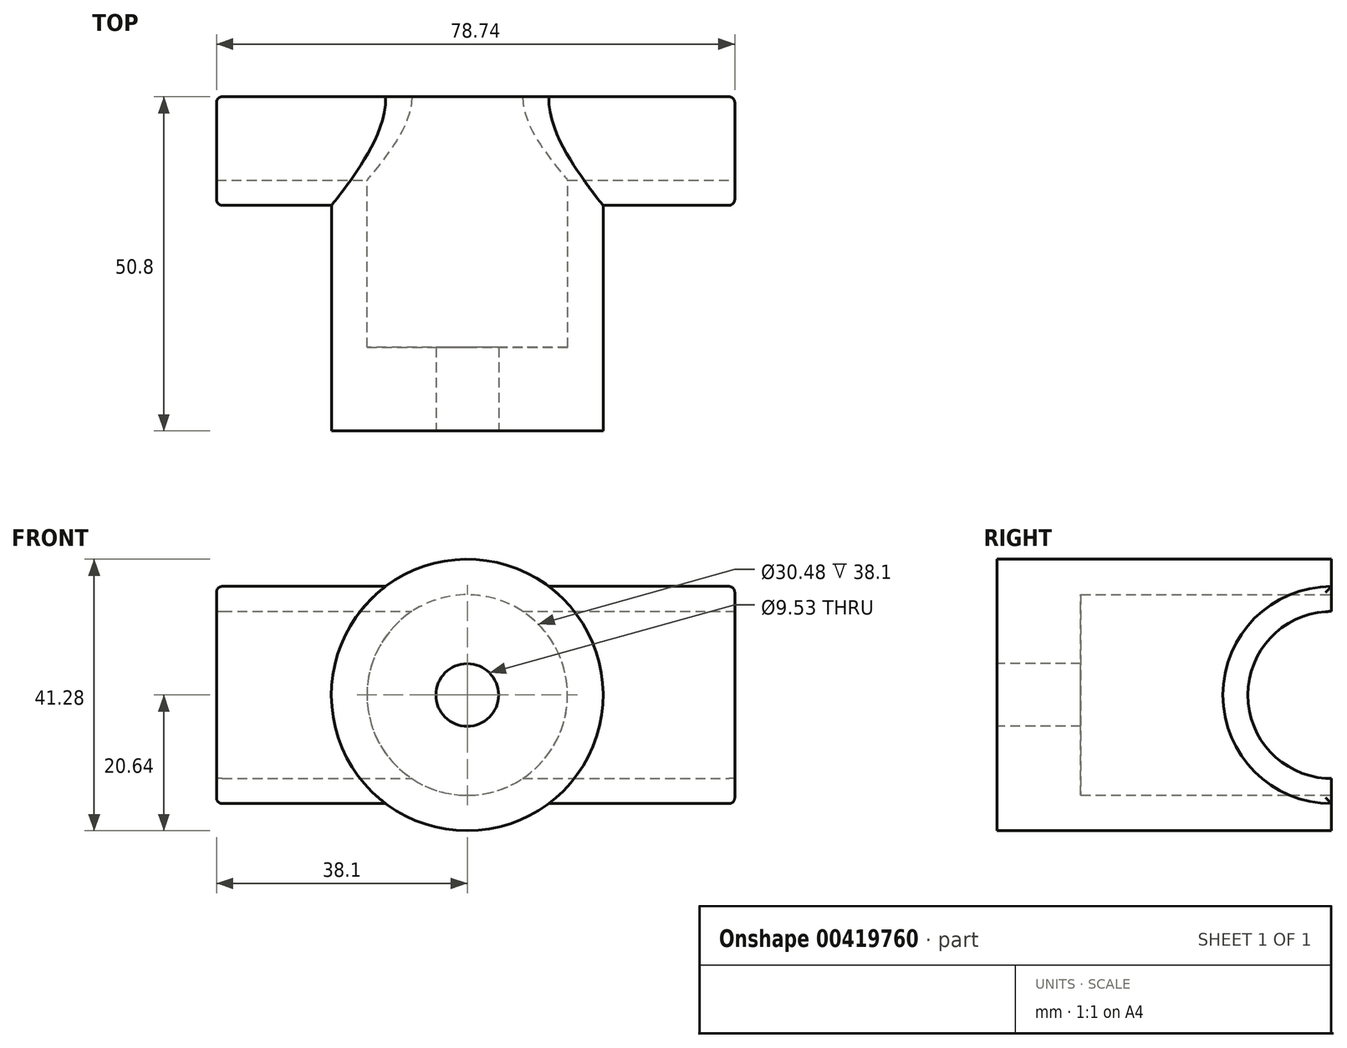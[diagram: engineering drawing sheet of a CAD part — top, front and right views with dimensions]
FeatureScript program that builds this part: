
annotation { "Feature Type Name" : "Feature", "Feature Type Description" : "" }
export const myFeature = defineFeature(function(context is Context, id is Id, definition is map)
    precondition{}
    {
        {
            var Q0;
            Q0=qCreatedBy(makeId("Front.planeOp"),FACE);
            var sketch = newSketch(context, id + "F0", { "sketchPlane" : qUnion([Q0])});
            skCircle(sketch, "E0", {"center": v(0, 0) * mm, "radius": 20.64 * mm});
            skSolve(sketch);
        }
        {
            var Q0;
            Q0 = qSketchRegion(id + "F0", true);
            extrude(context, id + "F1", {"entities" : qUnion([Q0]), "depth" : 50.8 * mm});
        }
        {
            var Q0;
            Q0=qCreatedBy(makeId("Right.planeOp"),FACE);
            cPlane(context, id + "F2", {"entities" : qUnion([Q0]), "cplaneType" : CPlaneType.OFFSET, "offset" : 40.64 * mm, "width" : 152.4 * mm, "height" : 152.4 * mm});
        }
        {
            var Q0;
            Q0=qCreatedBy(id+"F2.planeOp",FACE);
            var sketch = newSketch(context, id + "F3", { "sketchPlane" : qUnion([Q0])});
            skArc(sketch, "E1", {"start": v(0, 16.51) * mm, "mid": v(-16.51, 0) * mm, "end": v(0, -16.51) * mm});
            skArc(sketch, "E2", {"start": v(0, 12.7) * mm, "mid": v(-12.7, 0) * mm, "end": v(0, -12.7) * mm});
            skLineSegment(sketch, "E3", {"start": v(0, 16.51) * mm, "end": v(0, 12.7) * mm});
            skPoint(sketch, "E4.orphan", {"position": v(0, 24.9) * mm});
            skLineSegment(sketch, "E5.trimOffspring", {"start": v(0, -12.7) * mm, "end": v(0, -16.51) * mm});
            skSolve(sketch);
        }
        {
            var Q0;
            Q0=makeQuery(id+"F3.imprint","IMPRINT",FACE,{"disambiguationData":[TD([[makeQuery(id+"F3.imprint","IMPRINT",EDGE,{"derivedFrom":sQuery(id+"F3.wireOp",EDGE,"E1")}),1.0]])]});
            extrude(context, id + "F4", {"entities" : qUnion([Q0]), "operationType" : NewBodyOperationType.ADD, "oppositeDirection" : true, "depth" : 78.74 * mm});
        }
        {
            var Q0;
            Q0=qCreatedBy(makeId("Front.planeOp"),FACE);
            var sketch = newSketch(context, id + "F5", { "sketchPlane" : qUnion([Q0])});
            skCircle(sketch, "E6", {"center": v(0, 0) * mm, "radius": 15.24 * mm});
            skSolve(sketch);
        }
        {
            var Q0;
            Q0=makeQuery(id+"F5.imprint","IMPRINT",FACE,{"disambiguationData":[TD([[makeQuery(id+"F5.imprint","IMPRINT",EDGE,{"derivedFrom":sQuery(id+"F5.wireOp",EDGE,"E6")}),1.0]])]});
            extrude(context, id + "F6", {"entities" : qUnion([Q0]), "operationType" : NewBodyOperationType.REMOVE, "depth" : 38.1 * mm});
        }
        {
            var Q0;
            Q0=qCreatedBy(id+"F2.planeOp",FACE);
            var sketch = newSketch(context, id + "F7", { "sketchPlane" : qUnion([Q0])});
            skArc(sketch, "E7", {"start": v(0, 12.7) * mm, "mid": v(-12.7, 0) * mm, "end": v(0, -12.7) * mm});
            skPoint(sketch, "E8.orphan", {"position": v(0, 24.9) * mm});
            skLineSegment(sketch, "E9", {"start": v(0, 12.7) * mm, "end": v(0, -12.7) * mm});
            skSolve(sketch);
        }
        {
            var Q0;
            Q0=makeQuery(id+"F7.imprint","IMPRINT",FACE,{"disambiguationData":[TD([[makeQuery(id+"F7.imprint","IMPRINT",EDGE,{"derivedFrom":sQuery(id+"F7.wireOp",EDGE,"E7")}),1.0]])]});
            extrude(context, id + "F8", {"entities" : qUnion([Q0]), "operationType" : NewBodyOperationType.REMOVE, "endBound" : BoundingType.THROUGH_ALL, "oppositeDirection" : true, "depth" : 25.4 * mm});
        }
        {
            var Q0;
            Q0=makeQuery(id+"F1.opExtrude","CAP_FACE",FACE,{"disambiguationData":[OSD([sQuery(id+"F0.wireOp",EDGE,"E0")])],"isStart":false});
            var sketch = newSketch(context, id + "F9", { "sketchPlane" : qUnion([Q0])});
            skCircle(sketch, "E10", {"center": v(0, 0) * mm, "radius": 4.76 * mm});
            skSolve(sketch);
        }
        {
            var Q0;
            Q0 = qSketchRegion(id + "F9", true);
            extrude(context, id + "F10", {"entities" : qUnion([Q0]), "operationType" : NewBodyOperationType.REMOVE, "endBound" : BoundingType.THROUGH_ALL, "oppositeDirection" : true, "depth" : 25.4 * mm});
        }
        {
            var Q0;
            Q0=makeQuery(id+"F4.opExtrude","CAP_EDGE",EDGE,{"disambiguationData":[OSD([sQuery(id+"F3.wireOp",EDGE,"E5.trimOffspring")])],"isStart":false});
            var Q1;
            Q1=makeQuery(id+"F4.opExtrude","CAP_EDGE",EDGE,{"disambiguationData":[OSD([sQuery(id+"F3.wireOp",EDGE,"E3")])],"isStart":false});
            var Q2;
            Q2=makeQuery(id+"F4.opExtrude","CAP_EDGE",EDGE,{"disambiguationData":[OSD([sQuery(id+"F3.wireOp",EDGE,"E5.trimOffspring")])],"isStart":true});
            var Q3;
            Q3=makeQuery(id+"F4.opExtrude","CAP_EDGE",EDGE,{"disambiguationData":[OSD([sQuery(id+"F3.wireOp",EDGE,"E3")])],"isStart":true});
            var Q4;
            Q4=makeQuery(id+"F4.opExtrude","CAP_EDGE",EDGE,{"disambiguationData":[OSD([sQuery(id+"F3.wireOp",EDGE,"E1")])],"isStart":false});
            var Q5;
            Q5=makeQuery(id+"F4.opExtrude","CAP_EDGE",EDGE,{"disambiguationData":[OSD([sQuery(id+"F3.wireOp",EDGE,"E1")])],"isStart":true});
            fillet(context, id + "F11", {"entities" : qUnion([Q0, Q1, Q2, Q3, Q4, Q5]), "radius" : 0.89 * mm, "tangentPropagation" : true, "allowEdgeOverflow" : false});
        }
    });
